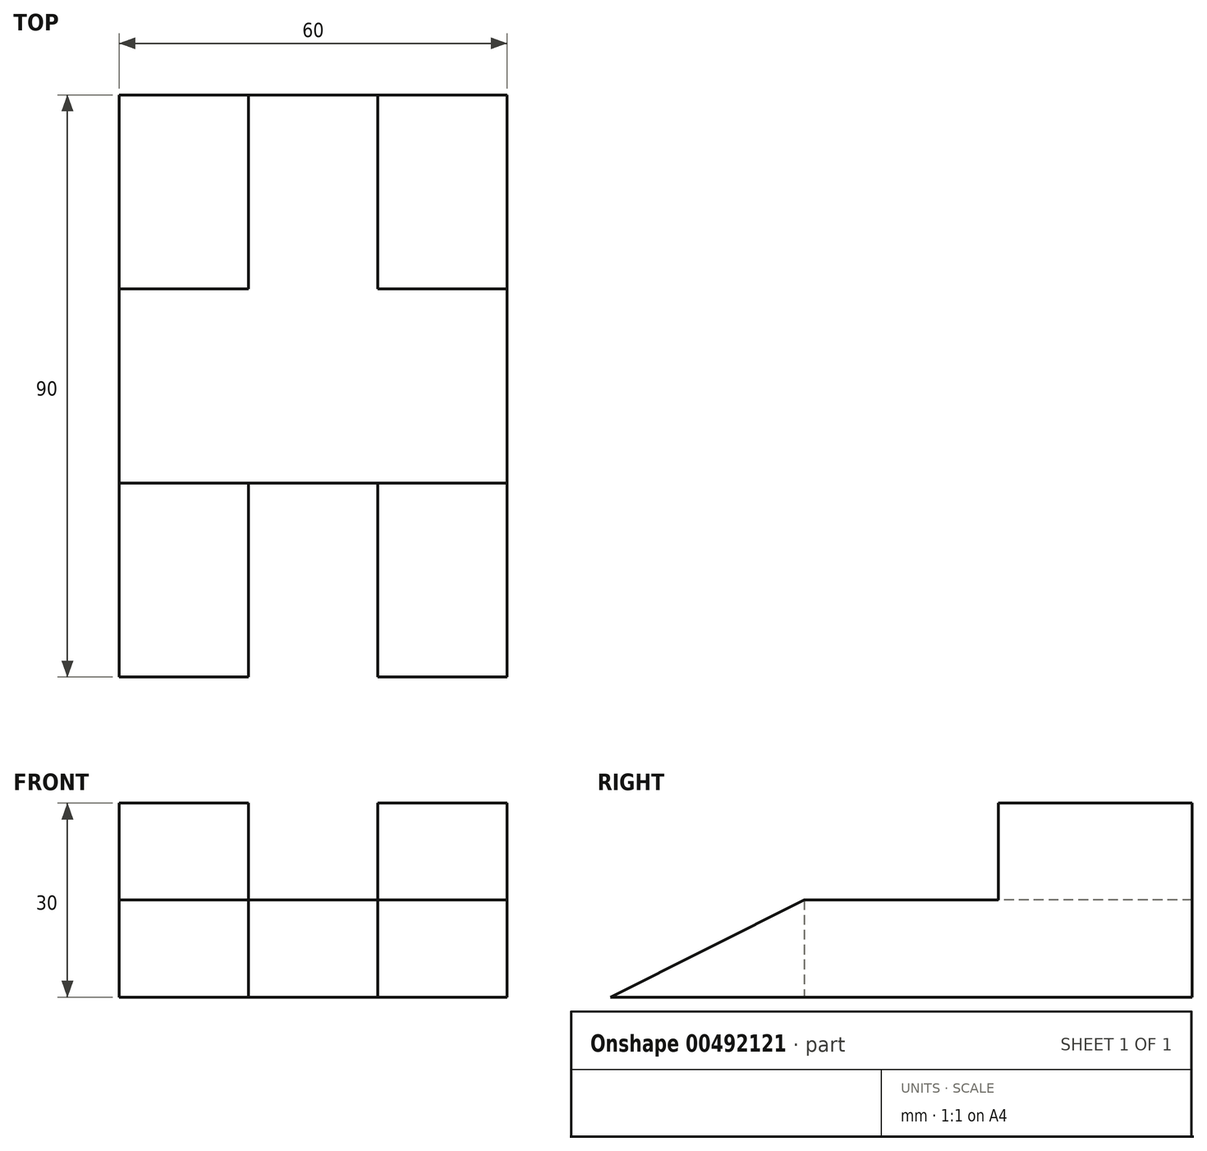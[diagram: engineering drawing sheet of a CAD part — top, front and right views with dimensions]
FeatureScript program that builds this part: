
annotation { "Feature Type Name" : "Feature", "Feature Type Description" : "" }
export const myFeature = defineFeature(function(context is Context, id is Id, definition is map)
    precondition{}
    {
        {
            var Q0;
            Q0=qCreatedBy(makeId("Top.planeOp"),FACE);
            var sketch = newSketch(context, id + "F0", { "sketchPlane" : qUnion([Q0])});
            skLineSegment(sketch, "E0.bottom", {"start": v(-60, 88.09) * mm, "end": v(0, 88.09) * mm});
            skLineSegment(sketch, "E0.top", {"start": v(-60, -1.91) * mm, "end": v(0, -1.91) * mm});
            skLineSegment(sketch, "E0.left", {"start": v(-60, 88.09) * mm, "end": v(-60, -1.91) * mm});
            skLineSegment(sketch, "E0.right", {"start": v(0, 88.09) * mm, "end": v(0, -1.91) * mm});
            skSolve(sketch);
        }
        {
            var Q0;
            Q0=makeQuery(id+"F0.imprint","IMPRINT",FACE,{"disambiguationData":[TD([[makeQuery(id+"F0.imprint","IMPRINT",EDGE,{"derivedFrom":sQuery(id+"F0.wireOp",EDGE,"E0.bottom")}),-1.0]])]});
            extrude(context, id + "F1", {"entities" : qUnion([Q0]), "depth" : 15 * mm});
        }
        {
            var Q0;
            Q0=makeQuery(id+"F1.opExtrude","CAP_FACE",FACE,{"disambiguationData":[OSD([sQuery(id+"F0.wireOp",EDGE,"E0.bottom"),sQuery(id+"F0.wireOp",EDGE,"E0.top"),sQuery(id+"F0.wireOp",EDGE,"E0.left"),sQuery(id+"F0.wireOp",EDGE,"E0.right")])],"isStart":false});
            var sketch = newSketch(context, id + "F2", { "sketchPlane" : qUnion([Q0])});
            skLineSegment(sketch, "E1.bottom", {"start": v(-60, 88.09) * mm, "end": v(-40, 88.09) * mm});
            skLineSegment(sketch, "E1.top", {"start": v(-60, 58.09) * mm, "end": v(-40, 58.09) * mm});
            skLineSegment(sketch, "E1.left", {"start": v(-60, 88.09) * mm, "end": v(-60, 58.09) * mm});
            skLineSegment(sketch, "E1.right", {"start": v(-40, 88.09) * mm, "end": v(-40, 58.09) * mm});
            skLineSegment(sketch, "E2.bottom", {"start": v(0, 88.09) * mm, "end": v(-20, 88.09) * mm});
            skLineSegment(sketch, "E2.top", {"start": v(0, 58.09) * mm, "end": v(-20, 58.09) * mm});
            skLineSegment(sketch, "E2.left", {"start": v(0, 88.09) * mm, "end": v(0, 58.09) * mm});
            skLineSegment(sketch, "E2.right", {"start": v(-20, 88.09) * mm, "end": v(-20, 58.09) * mm});
            skSolve(sketch);
        }
        {
            var Q0;
            Q0 = qSketchRegion(id + "F2", true);
            extrude(context, id + "F3", {"entities" : qUnion([Q0]), "operationType" : NewBodyOperationType.ADD, "depth" : 15 * mm});
        }
        {
            var Q0;
            Q0=makeQuery(id+"F3.boolean.opBoolean","MERGE",FACE,{"derivedFrom":[makeQuery(id+"F1.opExtrude","SWEPT_FACE",FACE,{"disambiguationData":[OSD([sQuery(id+"F0.wireOp",EDGE,"E0.right")])]}),makeQuery(id+"F3.opExtrude","SWEPT_FACE",FACE,{"disambiguationData":[OSD([sQuery(id+"F2.wireOp",EDGE,"E2.left")])]})]});
            var sketch = newSketch(context, id + "F4", { "sketchPlane" : qUnion([Q0])});
            skLineSegment(sketch, "E3", {"start": v(-1.91, 0) * mm, "end": v(28.09, 15) * mm});
            skLineSegment(sketch, "E4", {"start": v(28.09, 15) * mm, "end": v(-1.91, 15) * mm});
            skLineSegment(sketch, "E5", {"start": v(-1.91, 15) * mm, "end": v(-1.91, 0) * mm});
            skSolve(sketch);
        }
        {
            var Q0;
            Q0=makeQuery(id+"F4.imprint","IMPRINT",FACE,{"disambiguationData":[TD([[makeQuery(id+"F4.imprint","IMPRINT",EDGE,{"derivedFrom":sQuery(id+"F4.wireOp",EDGE,"E3")}),1.0]])]});
            extrude(context, id + "F5", {"entities" : qUnion([Q0]), "operationType" : NewBodyOperationType.REMOVE, "oppositeDirection" : true, "depth" : 60 * mm});
        }
        {
            var Q0;
            Q0=makeQuery(id+"F1.opExtrude","CAP_FACE",FACE,{"disambiguationData":[OSD([sQuery(id+"F0.wireOp",EDGE,"E0.bottom"),sQuery(id+"F0.wireOp",EDGE,"E0.top"),sQuery(id+"F0.wireOp",EDGE,"E0.left"),sQuery(id+"F0.wireOp",EDGE,"E0.right")])],"isStart":true});
            var sketch = newSketch(context, id + "F6", { "sketchPlane" : qUnion([Q0])});
            skLineSegment(sketch, "E6.bottom", {"start": v(-40, 1.91) * mm, "end": v(-20, 1.91) * mm});
            skLineSegment(sketch, "E6.top", {"start": v(-40, -28.09) * mm, "end": v(-20, -28.09) * mm});
            skLineSegment(sketch, "E6.left", {"start": v(-40, 1.91) * mm, "end": v(-40, -28.09) * mm});
            skLineSegment(sketch, "E6.right", {"start": v(-20, 1.91) * mm, "end": v(-20, -28.09) * mm});
            skSolve(sketch);
        }
        {
            var Q0;
            Q0=makeQuery(id+"F6.imprint","IMPRINT",FACE,{"disambiguationData":[TD([[makeQuery(id+"F6.imprint","IMPRINT",EDGE,{"derivedFrom":sQuery(id+"F6.wireOp",EDGE,"E6.bottom")}),-1.0]])]});
            extrude(context, id + "F7", {"entities" : qUnion([Q0]), "operationType" : NewBodyOperationType.REMOVE, "oppositeDirection" : true, "depth" : 15 * mm});
        }
    });
